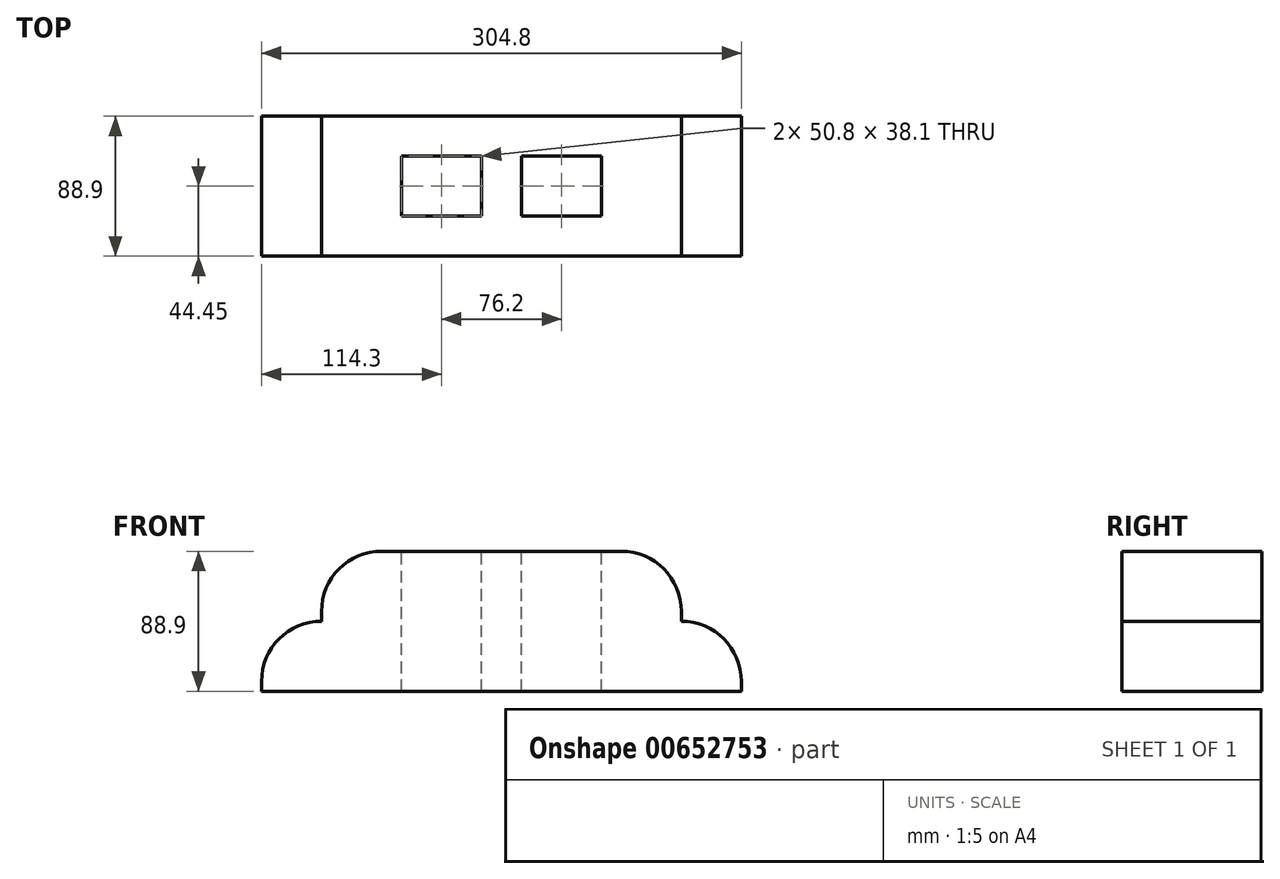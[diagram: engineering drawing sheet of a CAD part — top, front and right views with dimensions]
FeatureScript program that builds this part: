
annotation { "Feature Type Name" : "Feature", "Feature Type Description" : "" }
export const myFeature = defineFeature(function(context is Context, id is Id, definition is map)
    precondition{}
    {
        {
            var Q0;
            Q0=qCreatedBy(makeId("Front.planeOp"),FACE);
            var sketch = newSketch(context, id + "F0", { "sketchPlane" : qUnion([Q0])});
            skLineSegment(sketch, "E0.bottom", {"start": v(152.4, -44.45) * mm, "end": v(-152.4, -44.45) * mm});
            skLineSegment(sketch, "E0.top", {"start": v(76.2, 44.45) * mm, "end": v(-76.2, 44.45) * mm});
            skLineSegment(sketch, "E0.left", {"start": v(152.4, -44.45) * mm, "end": v(152.4, -38.1) * mm});
            skLineSegment(sketch, "E0.right", {"start": v(-152.4, -44.45) * mm, "end": v(-152.4, -38.1) * mm});
            skPoint(sketch, "E0.middle", {"position": v(0, 0) * mm});
            skLineSegment(sketch, "E1", {"start": v(114.3, 0) * mm, "end": v(114.3, 0) * mm});
            skLineSegment(sketch, "E2", {"start": v(-114.3, 6.35) * mm, "end": v(-114.3, 0) * mm});
            skPoint(sketch, "E3.newPointA", {"position": v(-152.4, 44.45) * mm});
            skArc(sketch, "E3.filletArc", {"start": v(-76.2, 44.45) * mm, "mid": v(-103.14, 33.3) * mm, "end": v(-114.3, 6.35) * mm});
            skPoint(sketch, "E4.orphan", {"position": v(-152.4, 0) * mm});
            skArc(sketch, "E5.filletArc", {"start": v(-114.3, 0) * mm, "mid": v(-141.24, -11.16) * mm, "end": v(-152.4, -38.1) * mm});
            skArc(sketch, "E6.MirrorCS", {"start": v(114.3, 0) * mm, "mid": v(141.24, -11.16) * mm, "end": v(152.4, -38.1) * mm});
            skArc(sketch, "E7.MirrorCS", {"start": v(76.2, 44.45) * mm, "mid": v(103.14, 33.3) * mm, "end": v(114.3, 6.35) * mm});
            skLineSegment(sketch, "E8.MirrorCS", {"start": v(114.3, 6.35) * mm, "end": v(114.3, 0) * mm});
            skPoint(sketch, "E9.orphan", {"position": v(152.4, 44.45) * mm});
            skPoint(sketch, "E10.orphan", {"position": v(152.4, 0) * mm});
            skSolve(sketch);
        }
        {
            var Q0;
            Q0=makeQuery(id+"F0.imprint","IMPRINT",FACE,{"disambiguationData":[TD([[makeQuery(id+"F0.imprint","IMPRINT",EDGE,{"derivedFrom":sQuery(id+"F0.wireOp",EDGE,"E0.bottom")}),-1.0]])]});
            extrude(context, id + "F1", {"entities" : qUnion([Q0]), "depth" : 88.9 * mm, "offsetDistance" : 25.4 * mm});
        }
        {
            var Q0;
            Q0=makeQuery(id+"F1.opExtrude","SWEPT_FACE",FACE,{"disambiguationData":[OSD([sQuery(id+"F0.wireOp",EDGE,"E0.top")])]});
            var sketch = newSketch(context, id + "F2", { "sketchPlane" : qUnion([Q0])});
            skLineSegment(sketch, "E11.0", {"start": v(-63.5, -63.5) * mm, "end": v(-63.5, -25.4) * mm});
            skLineSegment(sketch, "E12.0", {"start": v(-12.7, -63.5) * mm, "end": v(-12.7, -25.4) * mm});
            skLineSegment(sketch, "E13.MirrorCS", {"start": v(12.7, -63.5) * mm, "end": v(12.7, -25.4) * mm});
            skLineSegment(sketch, "E14.MirrorCS", {"start": v(63.5, -63.5) * mm, "end": v(63.5, -25.4) * mm});
            skLineSegment(sketch, "E15.0", {"start": v(63.5, -25.4) * mm, "end": v(12.7, -25.4) * mm});
            skLineSegment(sketch, "E16.0", {"start": v(82.55, 6.35) * mm, "end": v(-82.55, 6.35) * mm});
            skLineSegment(sketch, "E16.1", {"start": v(82.55, -95.25) * mm, "end": v(82.55, 6.35) * mm});
            skLineSegment(sketch, "E16.2", {"start": v(-82.55, -95.25) * mm, "end": v(82.55, -95.25) * mm});
            skLineSegment(sketch, "E16.3", {"start": v(-82.55, 6.35) * mm, "end": v(-82.55, -95.25) * mm});
            skLineSegment(sketch, "E17.0", {"start": v(63.5, -63.5) * mm, "end": v(12.7, -63.5) * mm});
            skPoint(sketch, "E18.orphan", {"position": v(-63.5, 0) * mm});
            skPoint(sketch, "E19.orphan", {"position": v(-63.5, -88.9) * mm});
            skPoint(sketch, "E20.orphan", {"position": v(-12.7, -88.9) * mm});
            skLineSegment(sketch, "E21.trimOffspring", {"start": v(-12.7, -63.5) * mm, "end": v(-63.5, -63.5) * mm});
            skLineSegment(sketch, "E22.trimOffspring", {"start": v(-12.7, -25.4) * mm, "end": v(-63.5, -25.4) * mm});
            skPoint(sketch, "E23.orphan", {"position": v(-12.7, 0) * mm});
            skPoint(sketch, "E24.orphan", {"position": v(12.7, 0) * mm});
            skPoint(sketch, "E25.orphan", {"position": v(63.5, 0) * mm});
            skPoint(sketch, "E26.orphan", {"position": v(63.5, -88.9) * mm});
            skPoint(sketch, "E27.orphan", {"position": v(12.7, -88.9) * mm});
            skSolve(sketch);
        }
        {
            var Q0;
            Q0=makeQuery(id+"F2.imprint","IMPRINT",FACE,{"disambiguationData":[TD([[makeQuery(id+"F2.imprint","IMPRINT",EDGE,{"derivedFrom":sQuery(id+"F2.wireOp",EDGE,"E11.0")}),-1.0]])]});
            var Q1;
            Q1=makeQuery(id+"F2.imprint","IMPRINT",FACE,{"disambiguationData":[TD([[makeQuery(id+"F2.imprint","IMPRINT",EDGE,{"derivedFrom":sQuery(id+"F2.wireOp",EDGE,"E13.MirrorCS")}),-1.0]])]});
            extrude(context, id + "F3", {"entities" : qUnion([Q0, Q1]), "operationType" : NewBodyOperationType.REMOVE, "endBound" : BoundingType.THROUGH_ALL, "oppositeDirection" : true, "depth" : 25.4 * mm, "offsetDistance" : 25.4 * mm});
        }
    });
